# Revit family: Domotics-DomesticRanges-GEWISS-SYSTEM_COMMAND-DIMMER_PUSH-BUTTON
name_source: partatom
category: Apparecchi elettrici
revit_build: Autodesk Revit 2016 (Build: 20161004_0715(x64)
units: mm (PartAtom-declared; Revit-internal decimal feet)

## family parameters
Condiviso = Sì
Host = Superficie
Mantenere orientamento annotazione = Sì
Punto di calcolo locali = Sì
Quota connettore circolare = Usa diametro
Taglio con vuoti quando caricato = Sì
Tipo di parte = Normale

## types (6) — shared parameters
Carico apparente = 0 VA
Catalogue = DOMOTICS
Catalogue Range = SYSTEM - DOMESTIC RANGE
Command = Push-button
Control = Push-button
Description. = Push-button dimmer
Electrocod = 0141
IDF = 32894165-b4c8-44ab-beb7-cb4eb3b257e9
IDT = 747644e9-8027-4257-a4c3-3235cb5c2112
Immagine tipo = GW21829.jpg
N. poli = 1
No. SYSTEM modules = 1
Produttore = GEWISS S.p.A.
Prospetto di default = 1219 mm
SEO = Dimmer
Supply voltage = 230V - 50 / 60 Hz
TIPO = System Dimmer Pulsante_GENERICO : GW21829 Dimmer per trasformatori elettronici 300W nero
Technical sheet = https://www.gewiss.com
Tipo simbolo = PULSANTI : DIMMPULS
URL = https://www.gewiss.com
Version file RFA = 19.4
Volt = 230 V

## per-type parameters (varying)
| type | Colour | Descrizione | EAN code | Inductive load | Inductive load 230V ac | Load 230V ac | Load type | Modello | Resistive load | Resistive load 230V ac |
| GW20828 - Dimmer for resist-induct. 500W white | White | DIMMER FOR RESIST-INDUCT. 500W SY.WHITE | 8011564747326 | 60-500 VA | 60-500 VA |  | Resistive/Inductive | GW20828 | 60-500 W | 60-500 W |
| GW20829 - Dimmer for electr.transf. 300W white | White | DIMMER FOR ELECTR.TRANSF. 300W SY.WHITE | 8011564747333 | 40-300 VA | 40-300 VA |  | Electronic transformers | GW20829 | 40-300 W | 40-300 W |
| GW21829 - Dimmer for electr.transf. 300W black | Black | DIMMER FOR ELECTR.TRANSF. 300W SY.BLACK | 8011564747357 | 40-300 VA | 40-300 VA |  | Electronic transformers | GW21829 | 40-300 W | 40-300 W |
| GW21828 - Dimmer for resist-induct. 500W black | Black | DIMMER FOR RESIST-INDUCT. 500W SY.BLACK | 8011564747340 | 60-500 VA | 60-500 VA |  | Resistive/Inductive | GW21828 | 60-500 W | 60-500 W |
| GW20818 - Elec.regul.air stirr. 230V 55-80VA white | White | ELEC.REGUL.AIR STIRR. 230V 55-80VA SY/WT | 8011564248922 |  |  | 55-80 VA | Air agitators | GW20818 |  |  |
| GW21818 - Elec.regul.air stirr. 230V 55-80VA black | Black | ELEC.REGUL.AIR STIRR. 230V 55-80VA SY/BK | 8011564248939 |  |  | 55-80 VA | Air agitators | GW21818 |  |  |

## geometry (parser evidence)
native form markers: Sweep x1
no freeform markers — native parametric forms only
